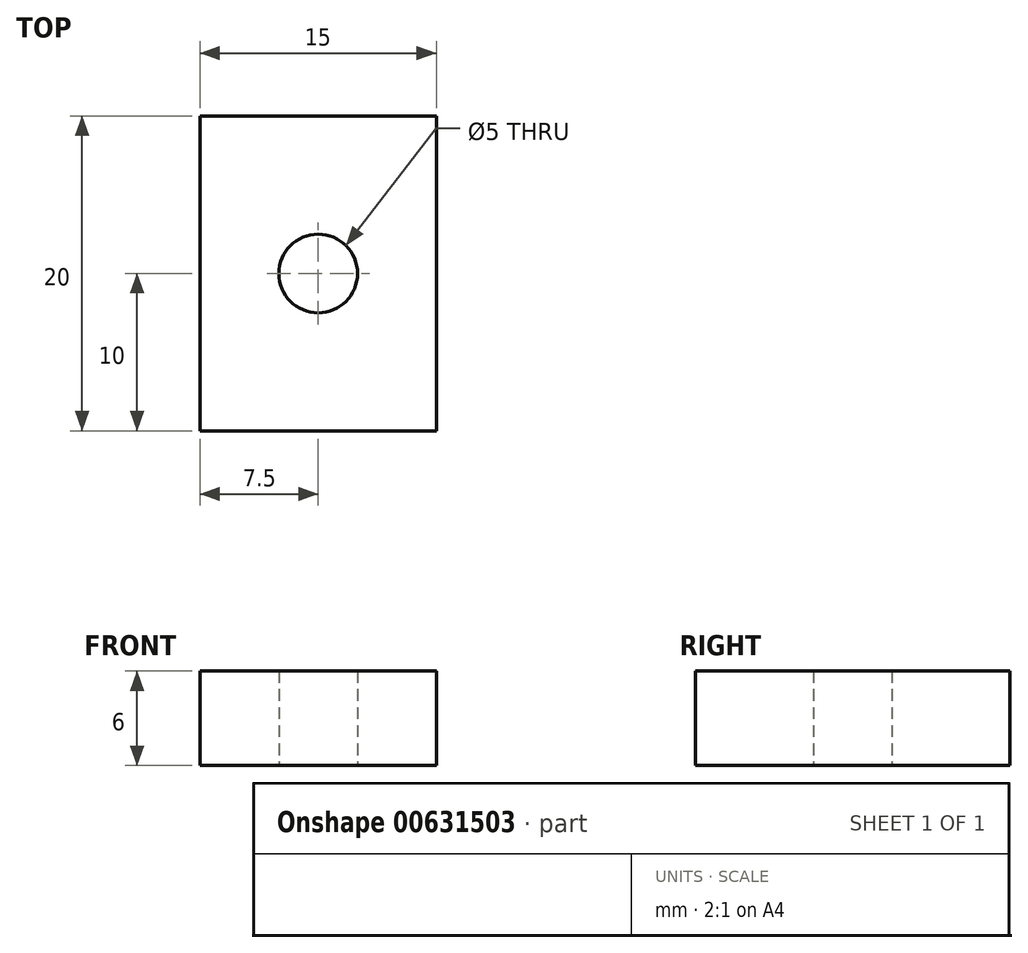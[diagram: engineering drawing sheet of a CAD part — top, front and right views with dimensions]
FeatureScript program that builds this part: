
annotation { "Feature Type Name" : "Feature", "Feature Type Description" : "" }
export const myFeature = defineFeature(function(context is Context, id is Id, definition is map)
    precondition{}
    {
        {
            var Q0;
            Q0=qCreatedBy(makeId("Top.planeOp"),FACE);
            var sketch = newSketch(context, id + "F0", { "sketchPlane" : qUnion([Q0])});
            skLineSegment(sketch, "E0.bottom", {"start": v(7.5, 10) * mm, "end": v(-7.5, 10) * mm});
            skLineSegment(sketch, "E0.top", {"start": v(7.5, -10) * mm, "end": v(-7.5, -10) * mm});
            skLineSegment(sketch, "E0.left", {"start": v(7.5, 10) * mm, "end": v(7.5, -10) * mm});
            skLineSegment(sketch, "E0.right", {"start": v(-7.5, 10) * mm, "end": v(-7.5, -10) * mm});
            skPoint(sketch, "E0.middle", {"position": v(0, 0) * mm});
            skCircle(sketch, "E1", {"center": v(0, 0) * mm, "radius": 2.5 * mm});
            skSolve(sketch);
        }
        {
            var Q0;
            Q0 = qSketchRegion(id + "F0", true);
            extrude(context, id + "F1", {"entities" : qUnion([Q0]), "depth" : 6 * mm, "offsetDistance" : 25 * mm});
        }
    });
